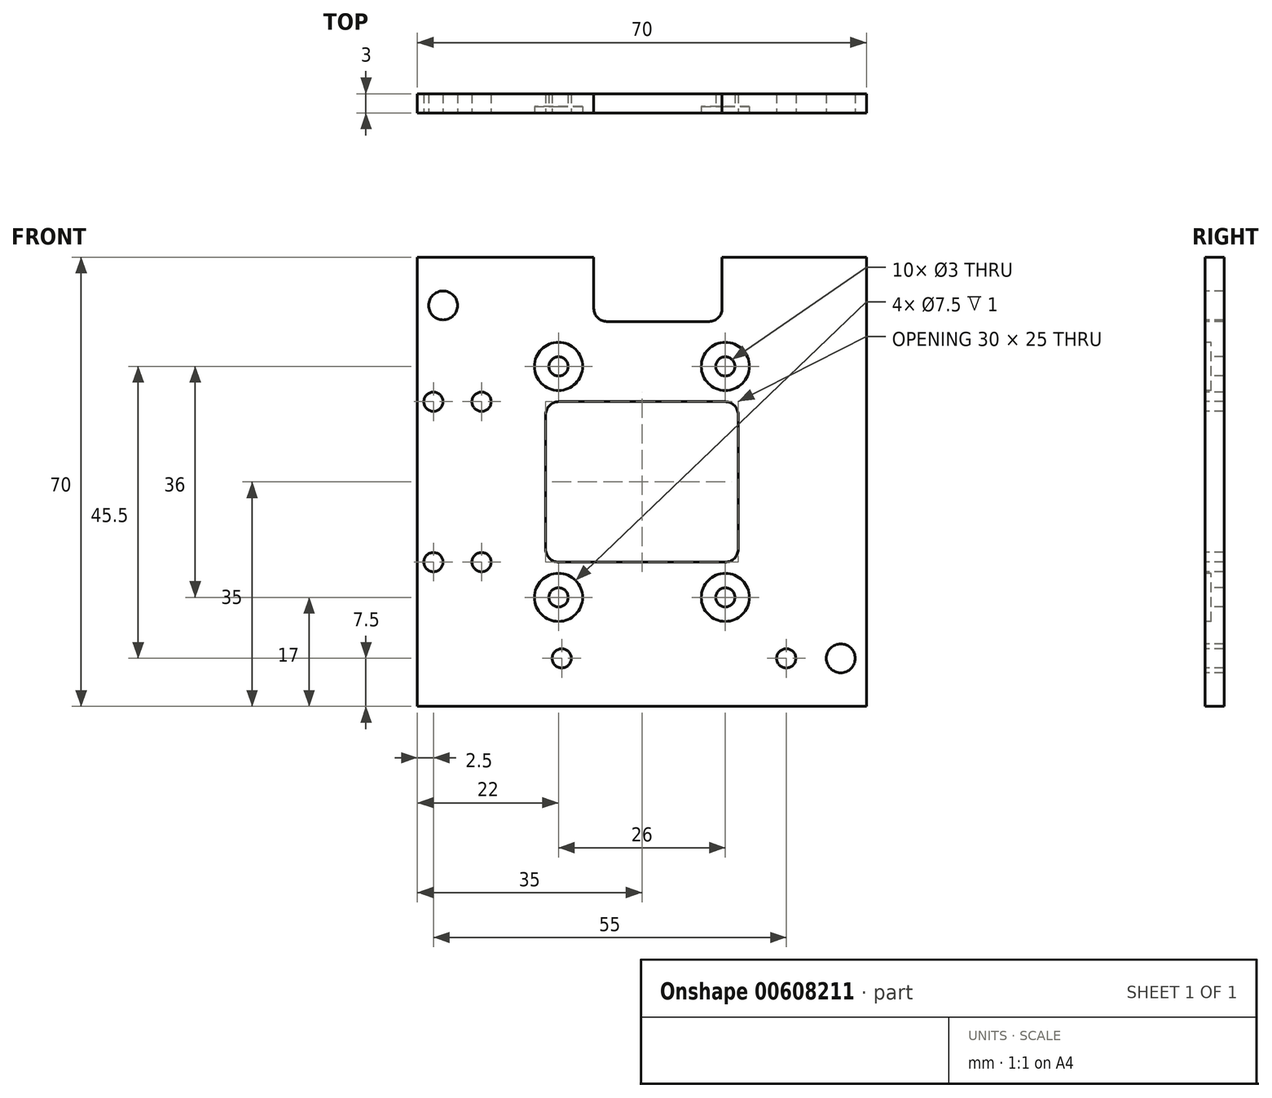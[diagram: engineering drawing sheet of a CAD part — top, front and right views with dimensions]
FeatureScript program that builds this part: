
annotation { "Feature Type Name" : "Feature", "Feature Type Description" : "" }
export const myFeature = defineFeature(function(context is Context, id is Id, definition is map)
    precondition{}
    {
        {
            var Q0;
            Q0=qCreatedBy(makeId("Front.planeOp"),FACE);
            var sketch = newSketch(context, id + "F0", { "sketchPlane" : qUnion([Q0])});
            skLineSegment(sketch, "E0.bottom", {"start": v(-35, 35) * mm, "end": v(35, 35) * mm});
            skLineSegment(sketch, "E0.top", {"start": v(-35, -35) * mm, "end": v(35, -35) * mm});
            skLineSegment(sketch, "E0.left", {"start": v(-35, 35) * mm, "end": v(-35, -35) * mm});
            skLineSegment(sketch, "E0.right", {"start": v(35, 35) * mm, "end": v(35, -35) * mm});
            skPoint(sketch, "E0.middle", {"position": v(0, 0) * mm});
            skSolve(sketch);
        }
        {
            var Q0;
            Q0=makeQuery(id+"F0.imprint","IMPRINT",FACE,{"disambiguationData":[TD([[makeQuery(id+"F0.imprint","IMPRINT",EDGE,{"derivedFrom":sQuery(id+"F0.wireOp",EDGE,"E0.bottom")}),-1.0]])]});
            extrude(context, id + "F1", {"entities" : qUnion([Q0]), "depth" : 3 * mm, "offsetDistance" : 25 * mm});
        }
        {
            var Q0;
            Q0=makeQuery(id+"F1.opExtrude","CAP_FACE",FACE,{"disambiguationData":[OSD([sQuery(id+"F0.wireOp",EDGE,"E0.bottom"),sQuery(id+"F0.wireOp",EDGE,"E0.top"),sQuery(id+"F0.wireOp",EDGE,"E0.left"),sQuery(id+"F0.wireOp",EDGE,"E0.right")])],"isStart":false});
            var sketch = newSketch(context, id + "F2", { "sketchPlane" : qUnion([Q0])});
            skCircle(sketch, "E1", {"center": v(-31, 27.5) * mm, "radius": 2.25 * mm});
            skCircle(sketch, "E2", {"center": v(31, -27.5) * mm, "radius": 2.25 * mm});
            skCircle(sketch, "E3", {"center": v(-13, 18) * mm, "radius": 1.5 * mm});
            skCircle(sketch, "E4", {"center": v(-13, -18) * mm, "radius": 1.5 * mm});
            skCircle(sketch, "E5.MirrorC", {"center": v(13, 18) * mm, "radius": 1.5 * mm});
            skCircle(sketch, "E6.MirrorC", {"center": v(13, -18) * mm, "radius": 1.5 * mm});
            skLineSegment(sketch, "E7.bottom", {"start": v(13, -12.5) * mm, "end": v(-13, -12.5) * mm});
            skLineSegment(sketch, "E7.top", {"start": v(13, 12.5) * mm, "end": v(-13, 12.5) * mm});
            skLineSegment(sketch, "E7.left", {"start": v(15, -10.5) * mm, "end": v(15, 10.5) * mm});
            skLineSegment(sketch, "E7.right", {"start": v(-15, -10.5) * mm, "end": v(-15, 10.5) * mm});
            skPoint(sketch, "E8.visualSharp", {"position": v(-15, 12.5) * mm});
            skArc(sketch, "E8.filletArc", {"start": v(-13, 12.5) * mm, "mid": v(-14.41, 11.91) * mm, "end": v(-15, 10.5) * mm});
            skPoint(sketch, "E9.visualSharp", {"position": v(15, 12.5) * mm});
            skArc(sketch, "E9.filletArc", {"start": v(15, 10.5) * mm, "mid": v(14.41, 11.91) * mm, "end": v(13, 12.5) * mm});
            skPoint(sketch, "E10.visualSharp", {"position": v(15, -12.5) * mm});
            skArc(sketch, "E10.filletArc", {"start": v(13, -12.5) * mm, "mid": v(14.41, -11.91) * mm, "end": v(15, -10.5) * mm});
            skPoint(sketch, "E11.visualSharp", {"position": v(-15, -12.5) * mm});
            skArc(sketch, "E11.filletArc", {"start": v(-15, -10.5) * mm, "mid": v(-14.41, -11.91) * mm, "end": v(-13, -12.5) * mm});
            skLineSegment(sketch, "E12.bottom", {"start": v(-7.5, 35) * mm, "end": v(12.5, 35) * mm});
            skLineSegment(sketch, "E12.top", {"start": v(-5.5, 25) * mm, "end": v(10.5, 25) * mm});
            skLineSegment(sketch, "E12.left", {"start": v(-7.5, 35) * mm, "end": v(-7.5, 27) * mm});
            skLineSegment(sketch, "E12.right", {"start": v(12.5, 35) * mm, "end": v(12.5, 27) * mm});
            skPoint(sketch, "E13.visualSharp", {"position": v(-7.5, 25) * mm});
            skArc(sketch, "E13.filletArc", {"start": v(-7.5, 27) * mm, "mid": v(-6.91, 25.59) * mm, "end": v(-5.5, 25) * mm});
            skPoint(sketch, "E14.visualSharp", {"position": v(12.5, 25) * mm});
            skArc(sketch, "E14.filletArc", {"start": v(10.5, 25) * mm, "mid": v(11.91, 25.59) * mm, "end": v(12.5, 27) * mm});
            skSolve(sketch);
        }
        {
            var Q0;
            Q0 = qSketchRegion(id + "F2", true);
            extrude(context, id + "F3", {"entities" : qUnion([Q0]), "operationType" : NewBodyOperationType.REMOVE, "endBound" : BoundingType.THROUGH_ALL, "oppositeDirection" : true, "depth" : 25 * mm, "offsetDistance" : 25 * mm});
        }
        {
            var Q0;
            Q0=makeQuery(id+"F1.opExtrude","CAP_FACE",FACE,{"disambiguationData":[OSD([sQuery(id+"F0.wireOp",EDGE,"E0.bottom"),sQuery(id+"F0.wireOp",EDGE,"E0.top"),sQuery(id+"F0.wireOp",EDGE,"E0.left"),sQuery(id+"F0.wireOp",EDGE,"E0.right")])],"isStart":false});
            var sketch = newSketch(context, id + "F4", { "sketchPlane" : qUnion([Q0])});
            skCircle(sketch, "E15", {"center": v(-13, 18) * mm, "radius": 3.75 * mm});
            skCircle(sketch, "E16.MirrorC", {"center": v(13, 18) * mm, "radius": 3.75 * mm});
            skCircle(sketch, "E17.MirrorC", {"center": v(-13, -18) * mm, "radius": 3.75 * mm});
            skCircle(sketch, "E18.MirrorC", {"center": v(13, -18) * mm, "radius": 3.75 * mm});
            skSolve(sketch);
        }
        {
            var Q0;
            Q0 = qSketchRegion(id + "F4", true);
            extrude(context, id + "F5", {"entities" : qUnion([Q0]), "operationType" : NewBodyOperationType.REMOVE, "oppositeDirection" : true, "depth" : 1 * mm, "offsetDistance" : 25 * mm});
        }
        {
            var Q0;
            Q0=makeQuery(id+"F1.opExtrude","CAP_FACE",FACE,{"disambiguationData":[OSD([sQuery(id+"F0.wireOp",EDGE,"E0.bottom"),sQuery(id+"F0.wireOp",EDGE,"E0.top"),sQuery(id+"F0.wireOp",EDGE,"E0.left"),sQuery(id+"F0.wireOp",EDGE,"E0.right")])],"isStart":false});
            var sketch = newSketch(context, id + "F6", { "sketchPlane" : qUnion([Q0])});
            skCircle(sketch, "E19", {"center": v(-12.5, -27.5) * mm, "radius": 1.5 * mm});
            skCircle(sketch, "E20", {"center": v(22.5, -27.5) * mm, "radius": 1.5 * mm});
            skSolve(sketch);
        }
        {
            var Q0;
            Q0 = qSketchRegion(id + "F6", true);
            extrude(context, id + "F7", {"entities" : qUnion([Q0]), "operationType" : NewBodyOperationType.REMOVE, "endBound" : BoundingType.THROUGH_ALL, "oppositeDirection" : true, "depth" : 25 * mm, "offsetDistance" : 25 * mm});
        }
        {
            var Q0;
            Q0=makeQuery(id+"F1.opExtrude","CAP_FACE",FACE,{"disambiguationData":[OSD([sQuery(id+"F0.wireOp",EDGE,"E0.bottom"),sQuery(id+"F0.wireOp",EDGE,"E0.top"),sQuery(id+"F0.wireOp",EDGE,"E0.left"),sQuery(id+"F0.wireOp",EDGE,"E0.right")])],"isStart":false});
            var sketch = newSketch(context, id + "F8", { "sketchPlane" : qUnion([Q0])});
            skCircle(sketch, "E21", {"center": v(-25, -12.5) * mm, "radius": 1.5 * mm});
            skCircle(sketch, "E22", {"center": v(-25, 12.5) * mm, "radius": 1.5 * mm});
            skCircle(sketch, "E23.MirrorC", {"center": v(-32.5, -12.5) * mm, "radius": 1.5 * mm});
            skCircle(sketch, "E24.MirrorC", {"center": v(-32.5, 12.5) * mm, "radius": 1.5 * mm});
            skSolve(sketch);
        }
        {
            var Q0;
            Q0 = qSketchRegion(id + "F8", true);
            extrude(context, id + "F9", {"entities" : qUnion([Q0]), "operationType" : NewBodyOperationType.REMOVE, "endBound" : BoundingType.THROUGH_ALL, "oppositeDirection" : true, "depth" : 25 * mm, "offsetDistance" : 25 * mm});
        }
    });
